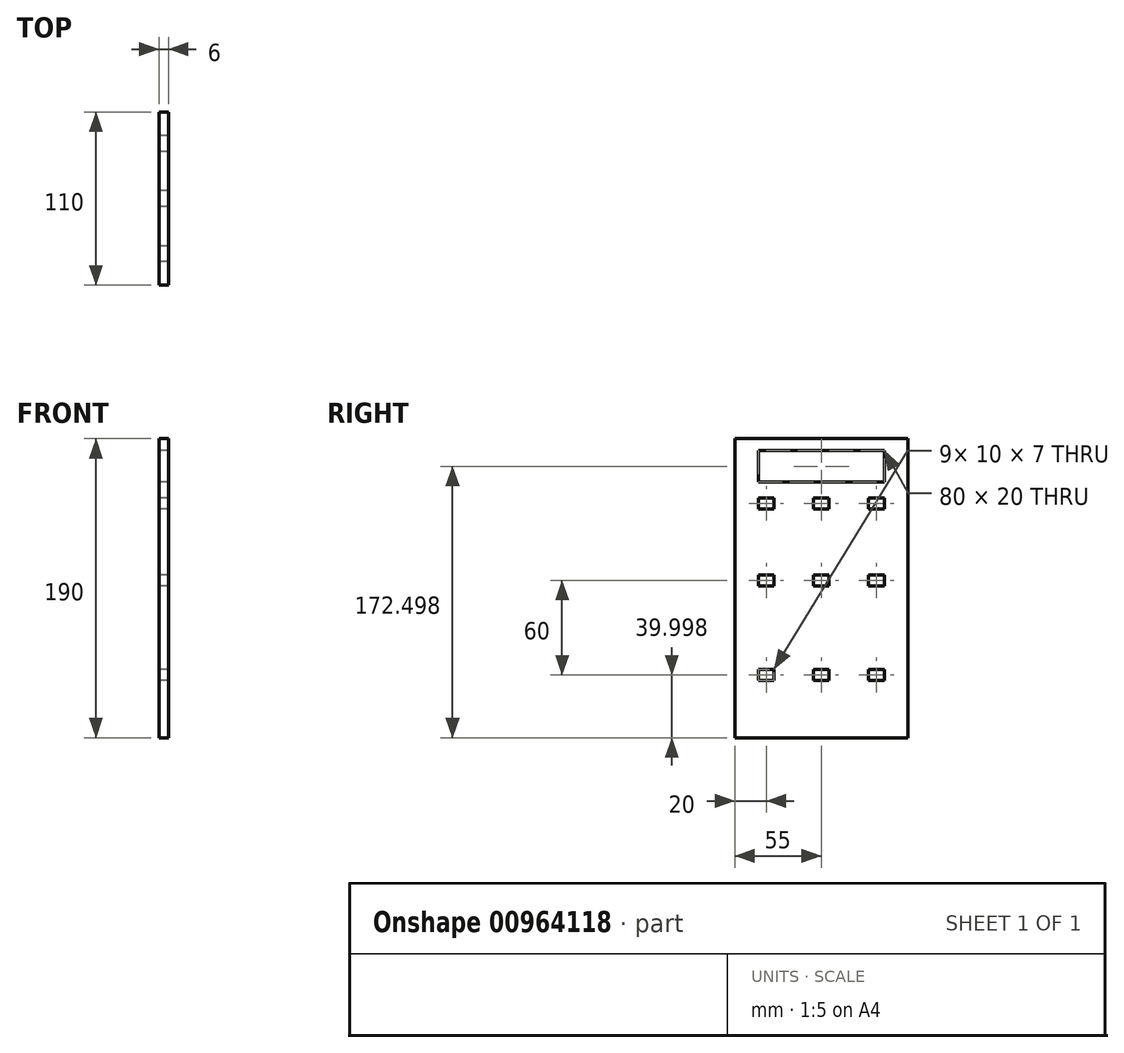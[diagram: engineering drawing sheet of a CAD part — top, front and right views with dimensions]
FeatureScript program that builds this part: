
annotation { "Feature Type Name" : "Feature", "Feature Type Description" : "" }
export const myFeature = defineFeature(function(context is Context, id is Id, definition is map)
    precondition{}
    {
        {
            var Q0;
            Q0=qCreatedBy(makeId("Right.planeOp"),FACE);
            var sketch = newSketch(context, id + "F0", { "sketchPlane" : qUnion([Q0])});
            skLineSegment(sketch, "E0.bottom", {"start": v(-47.5, 142.22) * mm, "end": v(62.5, 142.22) * mm});
            skLineSegment(sketch, "E0.top", {"start": v(-47.5, -47.78) * mm, "end": v(62.5, -47.78) * mm});
            skLineSegment(sketch, "E0.left", {"start": v(-47.5, 142.22) * mm, "end": v(-47.5, -47.78) * mm});
            skLineSegment(sketch, "E0.right", {"start": v(62.5, 142.22) * mm, "end": v(62.5, -47.78) * mm});
            skLineSegment(sketch, "E1.bottom", {"start": v(37.5, -4.28) * mm, "end": v(47.5, -4.28) * mm});
            skLineSegment(sketch, "E1.top", {"start": v(37.5, -11.28) * mm, "end": v(47.5, -11.28) * mm});
            skLineSegment(sketch, "E1.left", {"start": v(37.5, -4.28) * mm, "end": v(37.5, -11.28) * mm});
            skLineSegment(sketch, "E1.right", {"start": v(47.5, -4.28) * mm, "end": v(47.5, -11.28) * mm});
            skPoint(sketch, "E1.middle", {"position": v(42.5, -7.78) * mm});
            skLineSegment(sketch, "E2.bottom", {"start": v(2.5, -4.28) * mm, "end": v(12.5, -4.28) * mm});
            skLineSegment(sketch, "E2.top", {"start": v(2.5, -11.28) * mm, "end": v(12.5, -11.28) * mm});
            skLineSegment(sketch, "E2.left", {"start": v(2.5, -4.28) * mm, "end": v(2.5, -11.28) * mm});
            skLineSegment(sketch, "E2.right", {"start": v(12.5, -4.28) * mm, "end": v(12.5, -11.28) * mm});
            skPoint(sketch, "E2.middle", {"position": v(7.5, -7.78) * mm});
            skLineSegment(sketch, "E3.bottom", {"start": v(-22.5, -4.28) * mm, "end": v(-32.5, -4.28) * mm});
            skLineSegment(sketch, "E3.top", {"start": v(-22.5, -11.28) * mm, "end": v(-32.5, -11.28) * mm});
            skLineSegment(sketch, "E3.left", {"start": v(-22.5, -4.28) * mm, "end": v(-22.5, -11.28) * mm});
            skLineSegment(sketch, "E3.right", {"start": v(-32.5, -4.28) * mm, "end": v(-32.5, -11.28) * mm});
            skPoint(sketch, "E3.middle", {"position": v(-27.5, -7.78) * mm});
            skLineSegment(sketch, "E4", {"start": v(-27.5, -7.78) * mm, "end": v(42.5, -7.78) * mm});
            skLineSegment(sketch, "E5", {"start": v(-47.5, 145.37) * mm, "end": v(-32.5, 145.37) * mm});
            skLineSegment(sketch, "E6", {"start": v(62.5, 129.84) * mm, "end": v(47.5, 129.84) * mm});
            skLineSegment(sketch, "E7", {"start": v(9.43, 142.22) * mm, "end": v(9.43, 134.72) * mm});
            skLineSegment(sketch, "E8", {"start": v(9.43, 134.72) * mm, "end": v(-32.5, 134.72) * mm});
            skLineSegment(sketch, "E9", {"start": v(-32.5, 134.72) * mm, "end": v(-32.5, 114.72) * mm});
            skLineSegment(sketch, "E10", {"start": v(-32.5, 114.72) * mm, "end": v(47.5, 114.72) * mm});
            skLineSegment(sketch, "E11", {"start": v(47.5, 114.72) * mm, "end": v(47.5, 134.72) * mm});
            skLineSegment(sketch, "E12", {"start": v(47.5, 134.72) * mm, "end": v(9.43, 134.72) * mm});
            skLineSegment(sketch, "E13", {"start": v(30.25, -7.78) * mm, "end": v(30.25, 22.22) * mm});
            skLineSegment(sketch, "E14", {"start": v(30.25, 22.22) * mm, "end": v(-3.72, 22.22) * mm});
            skLineSegment(sketch, "E15.MirrorCS", {"start": v(37.5, 55.72) * mm, "end": v(47.5, 55.72) * mm});
            skLineSegment(sketch, "E16.MirrorCS", {"start": v(-32.5, 48.72) * mm, "end": v(-32.5, 55.72) * mm});
            skLineSegment(sketch, "E17.MirrorCS", {"start": v(37.5, 48.72) * mm, "end": v(37.5, 55.72) * mm});
            skLineSegment(sketch, "E18.MirrorCS", {"start": v(-22.5, 55.72) * mm, "end": v(-32.5, 55.72) * mm});
            skLineSegment(sketch, "E19.MirrorCS", {"start": v(2.5, 48.72) * mm, "end": v(2.5, 55.72) * mm});
            skLineSegment(sketch, "E20.MirrorCS", {"start": v(2.5, 55.72) * mm, "end": v(12.5, 55.72) * mm});
            skLineSegment(sketch, "E21.MirrorCS", {"start": v(37.5, 48.72) * mm, "end": v(47.5, 48.72) * mm});
            skLineSegment(sketch, "E22.MirrorCS", {"start": v(2.5, 48.72) * mm, "end": v(12.5, 48.72) * mm});
            skLineSegment(sketch, "E23.MirrorCS", {"start": v(-22.5, 48.72) * mm, "end": v(-22.5, 55.72) * mm});
            skLineSegment(sketch, "E24.MirrorCS", {"start": v(-22.5, 48.72) * mm, "end": v(-32.5, 48.72) * mm});
            skPoint(sketch, "E25.MirrorP", {"position": v(7.5, 52.22) * mm});
            skPoint(sketch, "E26.MirrorP", {"position": v(-27.5, 52.22) * mm});
            skPoint(sketch, "E27.MirrorP", {"position": v(42.5, 52.22) * mm});
            skLineSegment(sketch, "E28.MirrorCS", {"start": v(47.5, 48.72) * mm, "end": v(47.5, 55.72) * mm});
            skLineSegment(sketch, "E29.MirrorCS", {"start": v(-27.5, 52.22) * mm, "end": v(42.5, 52.22) * mm});
            skLineSegment(sketch, "E30.MirrorCS", {"start": v(12.5, 48.72) * mm, "end": v(12.5, 55.72) * mm});
            skLineSegment(sketch, "E31", {"start": v(24, 52.22) * mm, "end": v(24, 76.72) * mm});
            skLineSegment(sketch, "E32", {"start": v(24, 76.72) * mm, "end": v(-2.6, 76.72) * mm});
            skLineSegment(sketch, "E33.MirrorCS", {"start": v(-22.5, 97.72) * mm, "end": v(-32.5, 97.72) * mm});
            skLineSegment(sketch, "E34.MirrorCS", {"start": v(12.5, 104.72) * mm, "end": v(12.5, 97.72) * mm});
            skLineSegment(sketch, "E35.MirrorCS", {"start": v(37.5, 97.72) * mm, "end": v(47.5, 97.72) * mm});
            skLineSegment(sketch, "E36.MirrorCS", {"start": v(2.5, 97.72) * mm, "end": v(12.5, 97.72) * mm});
            skLineSegment(sketch, "E37.MirrorCS", {"start": v(2.5, 104.72) * mm, "end": v(12.5, 104.72) * mm});
            skLineSegment(sketch, "E38.MirrorCS", {"start": v(37.5, 104.72) * mm, "end": v(47.5, 104.72) * mm});
            skLineSegment(sketch, "E39.MirrorCS", {"start": v(-22.5, 104.72) * mm, "end": v(-22.5, 97.72) * mm});
            skPoint(sketch, "E40.MirrorP", {"position": v(42.5, 101.22) * mm});
            skLineSegment(sketch, "E41.MirrorCS", {"start": v(2.5, 104.72) * mm, "end": v(2.5, 97.72) * mm});
            skLineSegment(sketch, "E42.MirrorCS", {"start": v(47.5, 104.72) * mm, "end": v(47.5, 97.72) * mm});
            skLineSegment(sketch, "E43.MirrorCS", {"start": v(-32.5, 104.72) * mm, "end": v(-32.5, 97.72) * mm});
            skPoint(sketch, "E44.MirrorP", {"position": v(7.5, 101.22) * mm});
            skPoint(sketch, "E45.MirrorP", {"position": v(-27.5, 101.22) * mm});
            skLineSegment(sketch, "E46.MirrorCS", {"start": v(37.5, 104.72) * mm, "end": v(37.5, 97.72) * mm});
            skLineSegment(sketch, "E47.MirrorCS", {"start": v(-27.5, 101.22) * mm, "end": v(42.5, 101.22) * mm});
            skLineSegment(sketch, "E48.MirrorCS", {"start": v(-22.5, 104.72) * mm, "end": v(-32.5, 104.72) * mm});
            skSolve(sketch);
        }
        {
            var Q0;
            {var subQ1=sQuery(id+"F0.wireOp",EDGE,"E5");Q0=makeQuery(id+"F0.imprint","IMPRINT",FACE,{"disambiguationData":[TD([[makeQuery(id+"F0.imprint","IMPRINT",EDGE,{"derivedFrom":subQ1}),1.0]])]});}
            var Q1;
            {var subQ0=sQuery(id+"F0.wireOp",EDGE,"E6");Q1=makeQuery(id+"F0.imprint","IMPRINT",FACE,{"disambiguationData":[TD([[makeQuery(id+"F0.imprint","IMPRINT",EDGE,{"derivedFrom":subQ0}),-1.0]])]});}
            var Q2;
            {var subQ38=sQuery(id+"F0.wireOp",EDGE,"E0.top");Q2=makeQuery(id+"F0.imprint","IMPRINT",FACE,{"disambiguationData":[TD([[makeQuery(id+"F0.imprint","IMPRINT",EDGE,{"derivedFrom":subQ38}),1.0]])]});}
            extrude(context, id + "F1", {"entities" : qUnion([Q0, Q1, Q2]), "depth" : 6 * mm, "offsetDistance" : 25 * mm});
        }
    });
